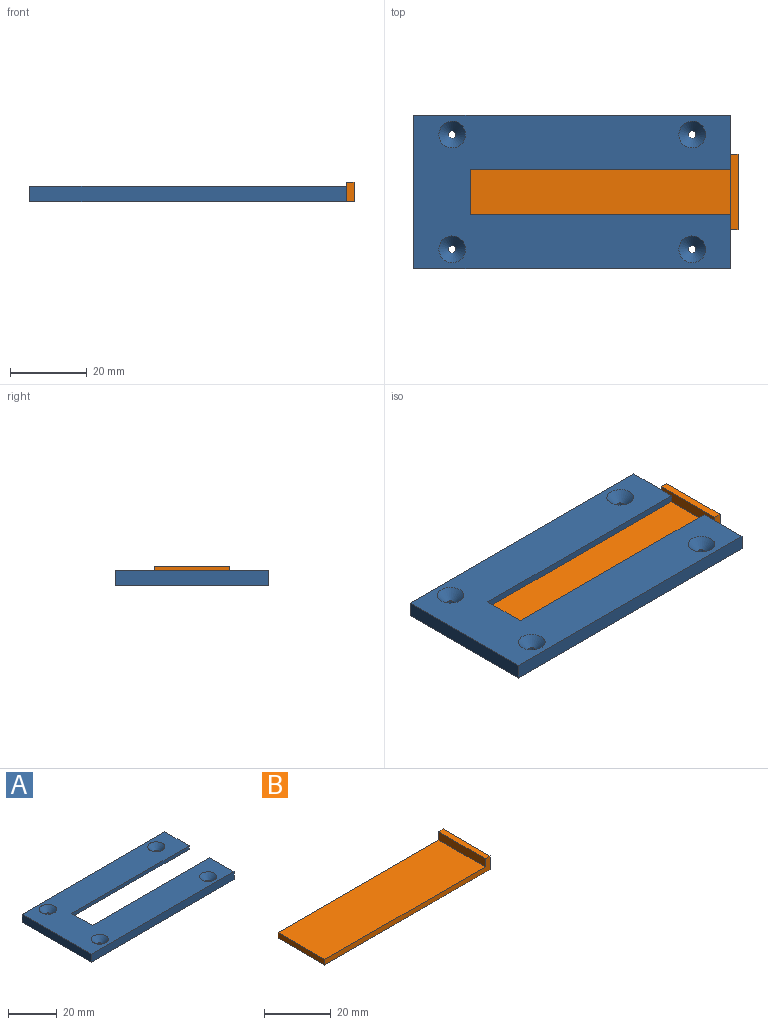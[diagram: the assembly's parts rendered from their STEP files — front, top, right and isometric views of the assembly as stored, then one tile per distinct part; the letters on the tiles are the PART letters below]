
ASSEMBLY  parts=2 mates=1
PART A: 22 faces, bbox 82.8x40x4 mm
  f0: plane 68x2.2mm, normal (0,1,0), area 149.6mm2, adj f1,f7,f9,f13
  f1: plane 20x4mm, normal (1,0,0), area 65.6mm2, adj f0,f2,f8,f9,f10,f11,f12,f13
  f2: plane 68x2.2mm, normal (0,-1,0), area 149.6mm2, adj f1,f3,f9,f11
  f3: plane 14x4mm, normal (1,0,0), area 47.2mm2, adj f2,f4,f8,f9,f10,f11
  f4: plane 82.75x4mm, normal (0,1,0), area 331mm2, adj f3,f5,f8,f9
  f5: plane 40x4mm, normal (-1,0,0), area 160mm2, adj f4,f6,f8,f9
  f6: plane 82.75x4mm, normal (0,-1,0), area 331mm2, adj f5,f7,f8,f9
  f7: plane 14x4mm, normal (1,0,0), area 47.2mm2, adj f0,f6,f8,f9,f12,f13
  f8: plane 82.75x40mm, normal (0,0,1), area 2340.1mm2, adj f1,f3,f4,f5,f6,f7,f10,f12
  f9: plane 82.75x40mm, normal (0,0,-1), area 1937.4mm2, adj f0,f1,f2,f3,f4,f5,f6,f7
  f10: plane 68x1.8mm, normal (0,-1,0), area 122.4mm2, adj f1,f3,f8,f11
  f11: plane 68x4mm, normal (0,0,-1), area 272mm2, adj f1,f2,f3,f10
  f12: plane 68x1.8mm, normal (0,1,0), area 122.4mm2, adj f1,f7,f8,f13
  f13: plane 68x4mm, normal (0,0,-1), area 272mm2, adj f0,f1,f7,f12
  f14: cylinder r=1mm len=2mm, axis (0,0,-1), area 9.4mm2, adj f9,f19
  f15: cylinder r=1mm len=2mm, axis (0,0,-1), area 9.4mm2, adj f9,f21
  f16: cylinder r=1mm len=2mm, axis (0,0,-1), area 9.4mm2, adj f9,f20
  f17: cylinder r=1mm len=2mm, axis (0,0,-1), area 9.4mm2, adj f9,f18
  f18: cone r=1mm half-angle=45deg, axis (0,0,1), area 50mm2, adj f8,f17
  f19: cone r=1mm half-angle=45deg, axis (0,0,1), area 50mm2, adj f8,f14
  f20: cone r=1mm half-angle=45deg, axis (0,0,1), area 50mm2, adj f8,f16
  f21: cone r=1mm half-angle=45deg, axis (0,0,1), area 50mm2, adj f8,f15
PART B: 8 faces, bbox 70x19.8x5 mm
  f0: plane 70x5mm, normal (0,-1,0), area 146mm2, adj f1,f3,f4,f5,f6,f7
  f1: plane 19.8x5mm, normal (1,0,0), area 99mm2, adj f0,f2,f5,f7
  f2: plane 70x5mm, normal (0,1,0), area 146mm2, adj f1,f3,f4,f5,f6,f7
  f3: plane 19.8x2mm, normal (-1,0,0), area 39.6mm2, adj f0,f2,f4,f5
  f4: plane 68x19.8mm, normal (0,0,1), area 1346.4mm2, adj f0,f2,f3,f6
  f5: plane 70x19.8mm, normal (0,0,-1), area 1386mm2, adj f0,f1,f2,f3
  f6: plane 19.8x3mm, normal (-1,0,0), area 59.4mm2, adj f0,f2,f4,f7
  f7: plane 19.8x2mm, normal (0,0,1), area 39.6mm2, adj f0,f1,f2,f6
PLACE A at identity fixed
PLACE B t=(0,-0.1,0)mm
MATE slider A.f1 <-> B.f3  axis (1,0,0) through (-35,-0.1,0)mm
